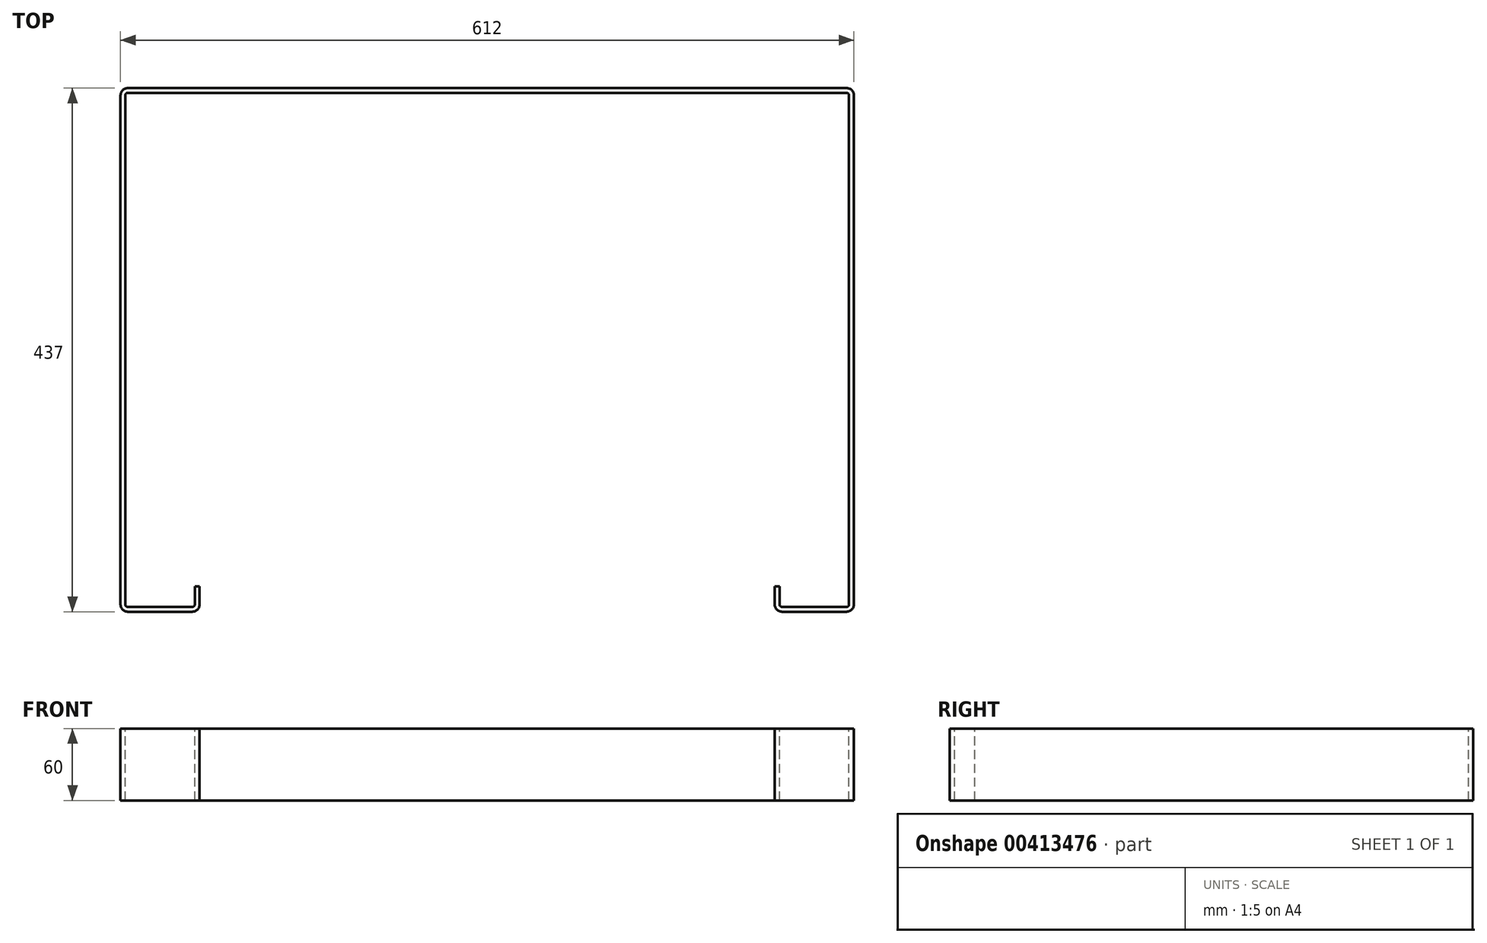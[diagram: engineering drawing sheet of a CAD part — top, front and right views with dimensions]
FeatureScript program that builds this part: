
annotation { "Feature Type Name" : "Feature", "Feature Type Description" : "" }
export const myFeature = defineFeature(function(context is Context, id is Id, definition is map)
    precondition{}
    {
        {
            var Q0;
            Q0=qCreatedBy(makeId("Top.planeOp"),FACE);
            var sketch = newSketch(context, id + "F0", { "sketchPlane" : qUnion([Q0])});
            skLineSegment(sketch, "E0.bottom", {"start": v(-300, 0) * mm, "end": v(-246, 0) * mm});
            skLineSegment(sketch, "E0.top", {"start": v(-300, 437) * mm, "end": v(300, 437) * mm});
            skLineSegment(sketch, "E0.left", {"start": v(-306, 6) * mm, "end": v(-306, 431) * mm});
            skLineSegment(sketch, "E0.right", {"start": v(306, 6) * mm, "end": v(306, 431) * mm});
            skPoint(sketch, "E1.visualSharp", {"position": v(-306, 437) * mm});
            skArc(sketch, "E1.filletArc", {"start": v(-300, 437) * mm, "mid": v(-304.24, 435.24) * mm, "end": v(-306, 431) * mm});
            skPoint(sketch, "E2.visualSharp", {"position": v(-306, 0) * mm});
            skArc(sketch, "E2.filletArc", {"start": v(-306, 6) * mm, "mid": v(-304.24, 1.76) * mm, "end": v(-300, 0) * mm});
            skPoint(sketch, "E3.visualSharp", {"position": v(306, 437) * mm});
            skArc(sketch, "E3.filletArc", {"start": v(306, 431) * mm, "mid": v(304.24, 435.24) * mm, "end": v(300, 437) * mm});
            skPoint(sketch, "E4.visualSharp", {"position": v(306, 0) * mm});
            skArc(sketch, "E4.filletArc", {"start": v(300, 0) * mm, "mid": v(304.24, 1.76) * mm, "end": v(306, 6) * mm});
            skLineSegment(sketch, "E5", {"start": v(246, 0) * mm, "end": v(300, 0) * mm});
            skLineSegment(sketch, "E6", {"start": v(-240, 6) * mm, "end": v(-240, 21) * mm});
            skArc(sketch, "E7.filletArc", {"start": v(-246, 0) * mm, "mid": v(-241.76, 1.76) * mm, "end": v(-240, 6) * mm});
            skLineSegment(sketch, "E8", {"start": v(240, 6) * mm, "end": v(240, 21) * mm});
            skArc(sketch, "E9.filletArc", {"start": v(240, 6) * mm, "mid": v(241.76, 1.76) * mm, "end": v(246, 0) * mm});
            skLineSegment(sketch, "E10.0", {"start": v(-302, 6) * mm, "end": v(-302, 431) * mm});
            skLineSegment(sketch, "E11.0", {"start": v(-300, 433) * mm, "end": v(300, 433) * mm});
            skLineSegment(sketch, "E12.0", {"start": v(302, 6) * mm, "end": v(302, 431) * mm});
            skLineSegment(sketch, "E13.0", {"start": v(246, 4) * mm, "end": v(300, 4) * mm});
            skLineSegment(sketch, "E14.0", {"start": v(-300, 4) * mm, "end": v(-246, 4) * mm});
            skLineSegment(sketch, "E15.0", {"start": v(-244, 6) * mm, "end": v(-244, 21) * mm});
            skLineSegment(sketch, "E16.0", {"start": v(244, 6) * mm, "end": v(244, 21) * mm});
            skArc(sketch, "E17.filletArc", {"start": v(244, 6) * mm, "mid": v(244.59, 4.59) * mm, "end": v(246, 4) * mm});
            skLineSegment(sketch, "E18", {"start": v(240, 21) * mm, "end": v(244, 21) * mm});
            skArc(sketch, "E19.filletArc", {"start": v(300, 4) * mm, "mid": v(301.41, 4.59) * mm, "end": v(302, 6) * mm});
            skArc(sketch, "E20.filletArc", {"start": v(302, 431) * mm, "mid": v(301.41, 432.41) * mm, "end": v(300, 433) * mm});
            skArc(sketch, "E21.filletArc", {"start": v(-300, 433) * mm, "mid": v(-301.41, 432.41) * mm, "end": v(-302, 431) * mm});
            skArc(sketch, "E22.filletArc", {"start": v(-302, 6) * mm, "mid": v(-301.41, 4.59) * mm, "end": v(-300, 4) * mm});
            skLineSegment(sketch, "E23", {"start": v(-240, 21) * mm, "end": v(-244, 21) * mm});
            skArc(sketch, "E24.filletArc", {"start": v(-246, 4) * mm, "mid": v(-244.59, 4.59) * mm, "end": v(-244, 6) * mm});
            skSolve(sketch);
        }
        {
            var Q0;
            Q0 = qSketchRegion(id + "F0", true);
            extrude(context, id + "F1", {"entities" : qUnion([Q0]), "oppositeDirection" : true, "depth" : 60 * mm});
        }
    });
